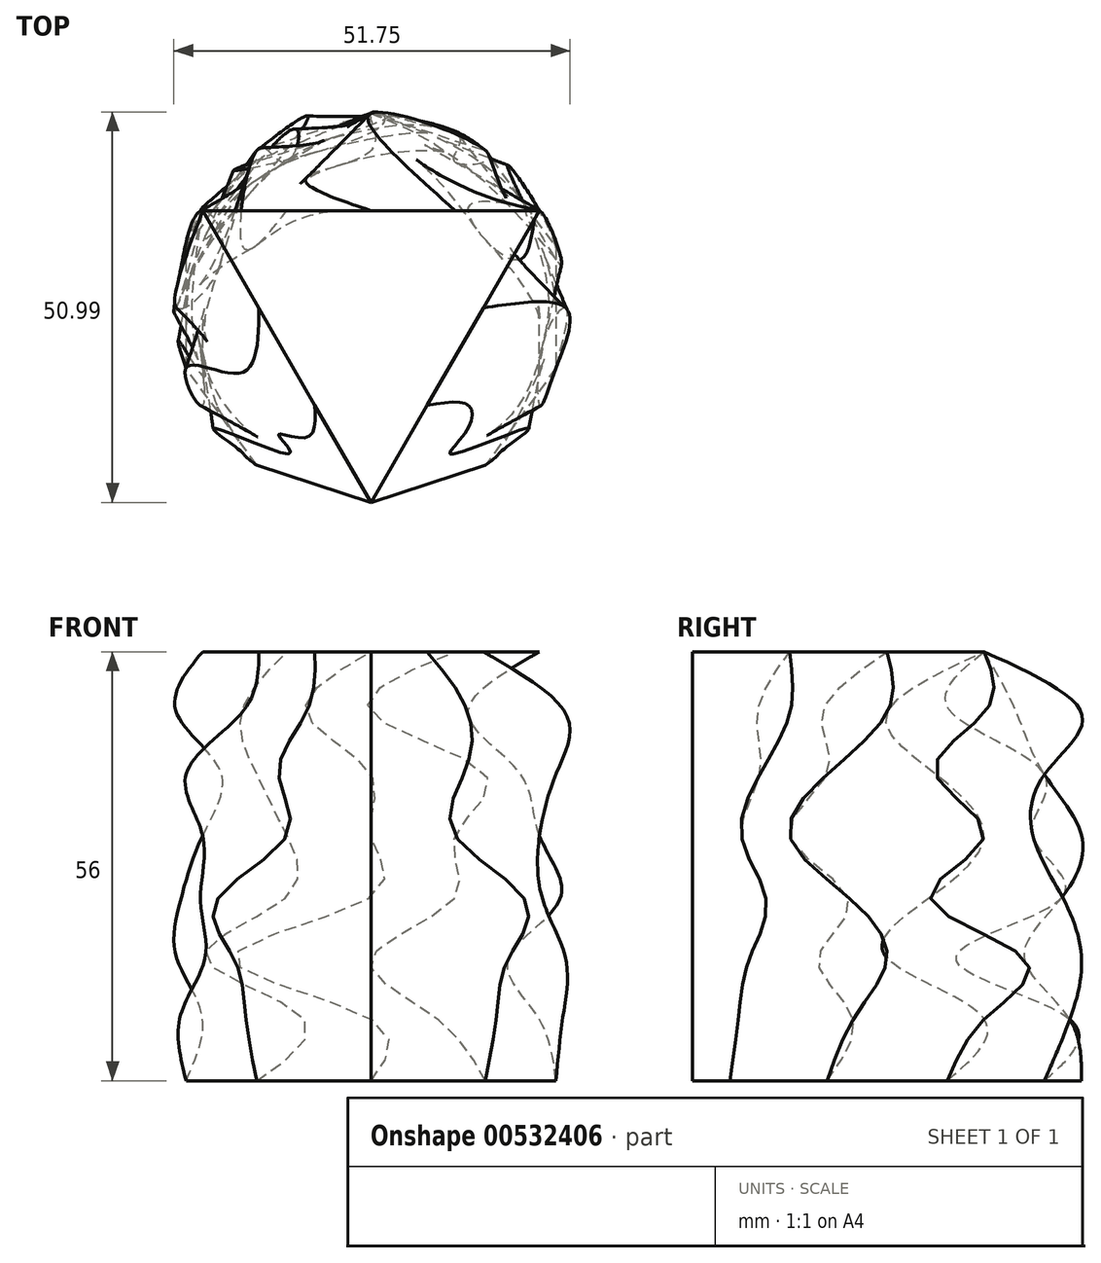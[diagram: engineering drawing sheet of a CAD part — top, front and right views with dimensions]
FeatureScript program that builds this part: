
annotation { "Feature Type Name" : "Feature", "Feature Type Description" : "" }
export const myFeature = defineFeature(function(context is Context, id is Id, definition is map)
    precondition{}
    {
        {
            assignVariable(context, id + "F0", {"name" : "pdist", "anyValue" : 8 * mm});
        }
        {
            var Q0;
            Q0=qCreatedBy(makeId("Top.planeOp"),FACE);
            cPlane(context, id + "F1", {"entities" : qUnion([Q0]), "cplaneType" : CPlaneType.OFFSET, "offset" : getVariable(context, 'pdist'), "width" : 152.4 * mm, "height" : 152.4 * mm});
        }
        {
            var Q0;
            Q0=qCreatedBy(id+"F1.planeOp",FACE);
            cPlane(context, id + "F2", {"entities" : qUnion([Q0]), "cplaneType" : CPlaneType.OFFSET, "offset" : getVariable(context, 'pdist'), "width" : 152.4 * mm, "height" : 152.4 * mm});
        }
        {
            var Q0;
            Q0=qCreatedBy(id+"F2.planeOp",FACE);
            cPlane(context, id + "F3", {"entities" : qUnion([Q0]), "cplaneType" : CPlaneType.OFFSET, "offset" : getVariable(context, 'pdist'), "width" : 152.4 * mm, "height" : 152.4 * mm});
        }
        {
            var Q0;
            Q0=qCreatedBy(id+"F3.planeOp",FACE);
            cPlane(context, id + "F4", {"entities" : qUnion([Q0]), "cplaneType" : CPlaneType.OFFSET, "offset" : getVariable(context, 'pdist'), "width" : 152.4 * mm, "height" : 152.4 * mm});
        }
        {
            var Q0;
            Q0=qCreatedBy(id+"F4.planeOp",FACE);
            cPlane(context, id + "F5", {"entities" : qUnion([Q0]), "cplaneType" : CPlaneType.OFFSET, "offset" : getVariable(context, 'pdist'), "width" : 152.4 * mm, "height" : 152.4 * mm});
        }
        {
            var Q0;
            Q0=qCreatedBy(id+"F5.planeOp",FACE);
            cPlane(context, id + "F6", {"entities" : qUnion([Q0]), "cplaneType" : CPlaneType.OFFSET, "offset" : getVariable(context, 'pdist'), "width" : 152.4 * mm, "height" : 152.4 * mm});
        }
        {
            var Q0;
            Q0=qCreatedBy(id+"F6.planeOp",FACE);
            cPlane(context, id + "F7", {"entities" : qUnion([Q0]), "cplaneType" : CPlaneType.OFFSET, "offset" : getVariable(context, 'pdist'), "width" : 152.4 * mm, "height" : 152.4 * mm});
        }
        {
            var Q0;
            Q0=qCreatedBy(id+"F7.planeOp",FACE);
            cPlane(context, id + "F8", {"entities" : qUnion([Q0]), "cplaneType" : CPlaneType.OFFSET, "offset" : getVariable(context, 'pdist'), "width" : 152.4 * mm, "height" : 152.4 * mm});
        }
        {
            var Q0;
            Q0=qCreatedBy(id+"F8.planeOp",FACE);
            cPlane(context, id + "F9", {"entities" : qUnion([Q0]), "cplaneType" : CPlaneType.OFFSET, "offset" : getVariable(context, 'pdist'), "width" : 152.4 * mm, "height" : 152.4 * mm});
        }
        {
            var Q0;
            Q0=qCreatedBy(makeId("Top.planeOp"),FACE);
            var sketch = newSketch(context, id + "F10", { "sketchPlane" : qUnion([Q0])});
            skPoint(sketch, "E0", {"position": v(0, -25.4) * mm});
            skCircle(sketch, "E1.cCircle", {"center": v(0, 0) * mm, "radius": 25.4 * mm, "construction": true});
            skLineSegment(sketch, "E1.0", {"start": v(0, -25.4) * mm, "end": v(-14.93, -20.55) * mm});
            skLineSegment(sketch, "E1.1", {"start": v(-14.93, -20.55) * mm, "end": v(-24.16, -7.85) * mm});
            skLineSegment(sketch, "E1.2", {"start": v(-24.16, -7.85) * mm, "end": v(-24.16, 7.85) * mm});
            skLineSegment(sketch, "E1.3", {"start": v(-24.16, 7.85) * mm, "end": v(-14.93, 20.55) * mm});
            skLineSegment(sketch, "E1.4", {"start": v(-14.93, 20.55) * mm, "end": v(0, 25.4) * mm});
            skLineSegment(sketch, "E1.5", {"start": v(0, 25.4) * mm, "end": v(14.93, 20.55) * mm});
            skLineSegment(sketch, "E1.6", {"start": v(14.93, 20.55) * mm, "end": v(24.16, 7.85) * mm});
            skLineSegment(sketch, "E1.7", {"start": v(24.16, 7.85) * mm, "end": v(24.16, -7.85) * mm});
            skLineSegment(sketch, "E1.8", {"start": v(24.16, -7.85) * mm, "end": v(14.93, -20.55) * mm});
            skLineSegment(sketch, "E1.9", {"start": v(14.93, -20.55) * mm, "end": v(0, -25.4) * mm});
            skSolve(sketch);
        }
        {
            var Q0;
            Q0=qCreatedBy(id+"F1.planeOp",FACE);
            var sketch = newSketch(context, id + "F11", { "sketchPlane" : qUnion([Q0])});
            skPoint(sketch, "E2.0", {"position": v(0, -25.4) * mm});
            skCircle(sketch, "E3.cCircle", {"center": v(0, 0) * mm, "radius": 25.4 * mm, "construction": true});
            skLineSegment(sketch, "E3.0", {"start": v(0, -25.4) * mm, "end": v(-16.33, -19.46) * mm});
            skLineSegment(sketch, "E3.1", {"start": v(-16.33, -19.46) * mm, "end": v(-25.01, -4.41) * mm});
            skLineSegment(sketch, "E3.2", {"start": v(-25.01, -4.41) * mm, "end": v(-22, 12.7) * mm});
            skLineSegment(sketch, "E3.3", {"start": v(-22, 12.7) * mm, "end": v(-8.69, 23.87) * mm});
            skLineSegment(sketch, "E3.4", {"start": v(-8.69, 23.87) * mm, "end": v(8.69, 23.87) * mm});
            skLineSegment(sketch, "E3.5", {"start": v(8.69, 23.87) * mm, "end": v(22, 12.7) * mm});
            skLineSegment(sketch, "E3.6", {"start": v(22, 12.7) * mm, "end": v(25.01, -4.41) * mm});
            skLineSegment(sketch, "E3.7", {"start": v(25.01, -4.41) * mm, "end": v(16.33, -19.46) * mm});
            skLineSegment(sketch, "E3.8", {"start": v(16.33, -19.46) * mm, "end": v(0, -25.4) * mm});
            skSolve(sketch);
        }
        {
            var Q0;
            Q0=qCreatedBy(id+"F2.planeOp",FACE);
            var sketch = newSketch(context, id + "F12", { "sketchPlane" : qUnion([Q0])});
            skPoint(sketch, "E4.0", {"position": v(0, 0) * mm});
            skPoint(sketch, "E5.0", {"position": v(0, -25.4) * mm});
            skCircle(sketch, "E6.cCircle", {"center": v(0, 0) * mm, "radius": 25.4 * mm, "construction": true});
            skLineSegment(sketch, "E6.0", {"start": v(0, -25.4) * mm, "end": v(-17.96, -17.96) * mm});
            skLineSegment(sketch, "E6.1", {"start": v(-17.96, -17.96) * mm, "end": v(-25.4, 0) * mm});
            skLineSegment(sketch, "E6.2", {"start": v(-25.4, 0) * mm, "end": v(-17.96, 17.96) * mm});
            skLineSegment(sketch, "E6.3", {"start": v(-17.96, 17.96) * mm, "end": v(0, 25.4) * mm});
            skLineSegment(sketch, "E6.4", {"start": v(0, 25.4) * mm, "end": v(17.96, 17.96) * mm});
            skLineSegment(sketch, "E6.5", {"start": v(17.96, 17.96) * mm, "end": v(25.4, 0) * mm});
            skLineSegment(sketch, "E6.6", {"start": v(25.4, 0) * mm, "end": v(17.96, -17.96) * mm});
            skLineSegment(sketch, "E6.7", {"start": v(17.96, -17.96) * mm, "end": v(0, -25.4) * mm});
            skSolve(sketch);
        }
        {
            var Q0;
            Q0=qCreatedBy(id+"F3.planeOp",FACE);
            var sketch = newSketch(context, id + "F13", { "sketchPlane" : qUnion([Q0])});
            skPoint(sketch, "E7.0", {"position": v(0, 0) * mm});
            skPoint(sketch, "E8.0", {"position": v(0, -25.4) * mm});
            skCircle(sketch, "E9.cCircle", {"center": v(0, 0) * mm, "radius": 25.4 * mm, "construction": true});
            skLineSegment(sketch, "E9.0", {"start": v(0, -25.4) * mm, "end": v(-19.86, -15.84) * mm});
            skLineSegment(sketch, "E9.1", {"start": v(-19.86, -15.84) * mm, "end": v(-24.76, 5.65) * mm});
            skLineSegment(sketch, "E9.2", {"start": v(-24.76, 5.65) * mm, "end": v(-11.02, 22.88) * mm});
            skLineSegment(sketch, "E9.3", {"start": v(-11.02, 22.88) * mm, "end": v(11.02, 22.88) * mm});
            skLineSegment(sketch, "E9.4", {"start": v(11.02, 22.88) * mm, "end": v(24.76, 5.65) * mm});
            skLineSegment(sketch, "E9.5", {"start": v(24.76, 5.65) * mm, "end": v(19.86, -15.84) * mm});
            skLineSegment(sketch, "E9.6", {"start": v(19.86, -15.84) * mm, "end": v(0, -25.4) * mm});
            skSolve(sketch);
        }
        {
            var Q0;
            Q0=qCreatedBy(id+"F4.planeOp",FACE);
            var sketch = newSketch(context, id + "F14", { "sketchPlane" : qUnion([Q0])});
            skPoint(sketch, "E10.0", {"position": v(0, 0) * mm});
            skPoint(sketch, "E11.0", {"position": v(0, -25.4) * mm});
            skCircle(sketch, "E12.cCircle", {"center": v(0, 0) * mm, "radius": 25.4 * mm, "construction": true});
            skLineSegment(sketch, "E12.0", {"start": v(0, -25.4) * mm, "end": v(-22, -12.7) * mm});
            skLineSegment(sketch, "E12.1", {"start": v(-22, -12.7) * mm, "end": v(-22, 12.7) * mm});
            skLineSegment(sketch, "E12.2", {"start": v(-22, 12.7) * mm, "end": v(0, 25.4) * mm});
            skLineSegment(sketch, "E12.3", {"start": v(0, 25.4) * mm, "end": v(22, 12.7) * mm});
            skLineSegment(sketch, "E12.4", {"start": v(22, 12.7) * mm, "end": v(22, -12.7) * mm});
            skLineSegment(sketch, "E12.5", {"start": v(22, -12.7) * mm, "end": v(0, -25.4) * mm});
            skSolve(sketch);
        }
        {
            var Q0;
            Q0=qCreatedBy(id+"F5.planeOp",FACE);
            var sketch = newSketch(context, id + "F15", { "sketchPlane" : qUnion([Q0])});
            skPoint(sketch, "E13.0", {"position": v(0, 0) * mm});
            skPoint(sketch, "E14.0", {"position": v(0, -25.4) * mm});
            skCircle(sketch, "E15.cCircle", {"center": v(0, 0) * mm, "radius": 25.4 * mm, "construction": true});
            skLineSegment(sketch, "E15.0", {"start": v(0, -25.4) * mm, "end": v(-24.16, -7.85) * mm});
            skLineSegment(sketch, "E15.1", {"start": v(-24.16, -7.85) * mm, "end": v(-14.93, 20.55) * mm});
            skLineSegment(sketch, "E15.2", {"start": v(-14.93, 20.55) * mm, "end": v(14.93, 20.55) * mm});
            skLineSegment(sketch, "E15.3", {"start": v(14.93, 20.55) * mm, "end": v(24.16, -7.85) * mm});
            skLineSegment(sketch, "E15.4", {"start": v(24.16, -7.85) * mm, "end": v(0, -25.4) * mm});
            skSolve(sketch);
        }
        {
            var Q0;
            Q0=qCreatedBy(id+"F6.planeOp",FACE);
            var sketch = newSketch(context, id + "F16", { "sketchPlane" : qUnion([Q0])});
            skPoint(sketch, "E16.0", {"position": v(0, 0) * mm});
            skPoint(sketch, "E17.0", {"position": v(0, -25.4) * mm});
            skCircle(sketch, "E18.cCircle", {"center": v(0, 0) * mm, "radius": 25.4 * mm, "construction": true});
            skLineSegment(sketch, "E18.0", {"start": v(0, -25.4) * mm, "end": v(-25.4, 0) * mm});
            skLineSegment(sketch, "E18.1", {"start": v(-25.4, 0) * mm, "end": v(0, 25.4) * mm});
            skLineSegment(sketch, "E18.2", {"start": v(0, 25.4) * mm, "end": v(25.4, 0) * mm});
            skLineSegment(sketch, "E18.3", {"start": v(25.4, 0) * mm, "end": v(0, -25.4) * mm});
            skSolve(sketch);
        }
        {
            var Q0;
            Q0=qCreatedBy(id+"F7.planeOp",FACE);
            var sketch = newSketch(context, id + "F17", { "sketchPlane" : qUnion([Q0])});
            skPoint(sketch, "E19.0", {"position": v(0, 0) * mm});
            skPoint(sketch, "E20.0", {"position": v(0, -25.4) * mm});
            skCircle(sketch, "E21.cCircle", {"center": v(0, 0) * mm, "radius": 25.4 * mm, "construction": true});
            skLineSegment(sketch, "E21.0", {"start": v(0, -25.4) * mm, "end": v(-22, 12.7) * mm});
            skLineSegment(sketch, "E21.1", {"start": v(-22, 12.7) * mm, "end": v(22, 12.7) * mm});
            skLineSegment(sketch, "E21.2", {"start": v(22, 12.7) * mm, "end": v(0, -25.4) * mm});
            skSolve(sketch);
        }
        {
            var Q0;
            Q0=makeQuery(id+"F10.imprint","IMPRINT",FACE,{"disambiguationData":[TD([[makeQuery(id+"F10.imprint","IMPRINT",EDGE,{"derivedFrom":sQuery(id+"F10.wireOp",EDGE,"E1.0")}),-1.0]])]});
            var Q1;
            Q1=makeQuery(id+"F11.imprint","IMPRINT",FACE,{"disambiguationData":[TD([[makeQuery(id+"F11.imprint","IMPRINT",EDGE,{"derivedFrom":sQuery(id+"F11.wireOp",EDGE,"E3.0")}),-1.0]])]});
            var Q2;
            Q2=makeQuery(id+"F12.imprint","IMPRINT",FACE,{"disambiguationData":[TD([[makeQuery(id+"F12.imprint","IMPRINT",EDGE,{"derivedFrom":sQuery(id+"F12.wireOp",EDGE,"E6.0")}),-1.0]])]});
            var Q3;
            Q3=makeQuery(id+"F13.imprint","IMPRINT",FACE,{"disambiguationData":[TD([[makeQuery(id+"F13.imprint","IMPRINT",EDGE,{"derivedFrom":sQuery(id+"F13.wireOp",EDGE,"E9.0")}),-1.0]])]});
            var Q4;
            Q4=makeQuery(id+"F14.imprint","IMPRINT",FACE,{"disambiguationData":[TD([[makeQuery(id+"F14.imprint","IMPRINT",EDGE,{"derivedFrom":sQuery(id+"F14.wireOp",EDGE,"E12.0")}),-1.0]])]});
            var Q5;
            Q5=makeQuery(id+"F15.imprint","IMPRINT",FACE,{"disambiguationData":[TD([[makeQuery(id+"F15.imprint","IMPRINT",EDGE,{"derivedFrom":sQuery(id+"F15.wireOp",EDGE,"E15.0")}),-1.0]])]});
            var Q6;
            Q6=makeQuery(id+"F16.imprint","IMPRINT",FACE,{"disambiguationData":[TD([[makeQuery(id+"F16.imprint","IMPRINT",EDGE,{"derivedFrom":sQuery(id+"F16.wireOp",EDGE,"E18.0")}),-1.0]])]});
            var Q7;
            Q7=makeQuery(id+"F17.imprint","IMPRINT",FACE,{"disambiguationData":[TD([[makeQuery(id+"F17.imprint","IMPRINT",EDGE,{"derivedFrom":sQuery(id+"F17.wireOp",EDGE,"E21.0")}),-1.0]])]});
            loft(context, id + "F18", {"sheetProfilesArray" : [{ "sheetProfileEntities" : qUnion([Q0]) }, { "sheetProfileEntities" : qUnion([Q1]) }, { "sheetProfileEntities" : qUnion([Q2]) }, { "sheetProfileEntities" : qUnion([Q3]) }, { "sheetProfileEntities" : qUnion([Q4]) }, { "sheetProfileEntities" : qUnion([Q5]) }, { "sheetProfileEntities" : qUnion([Q6]) }, { "sheetProfileEntities" : qUnion([Q7]) }]});
        }
    });
